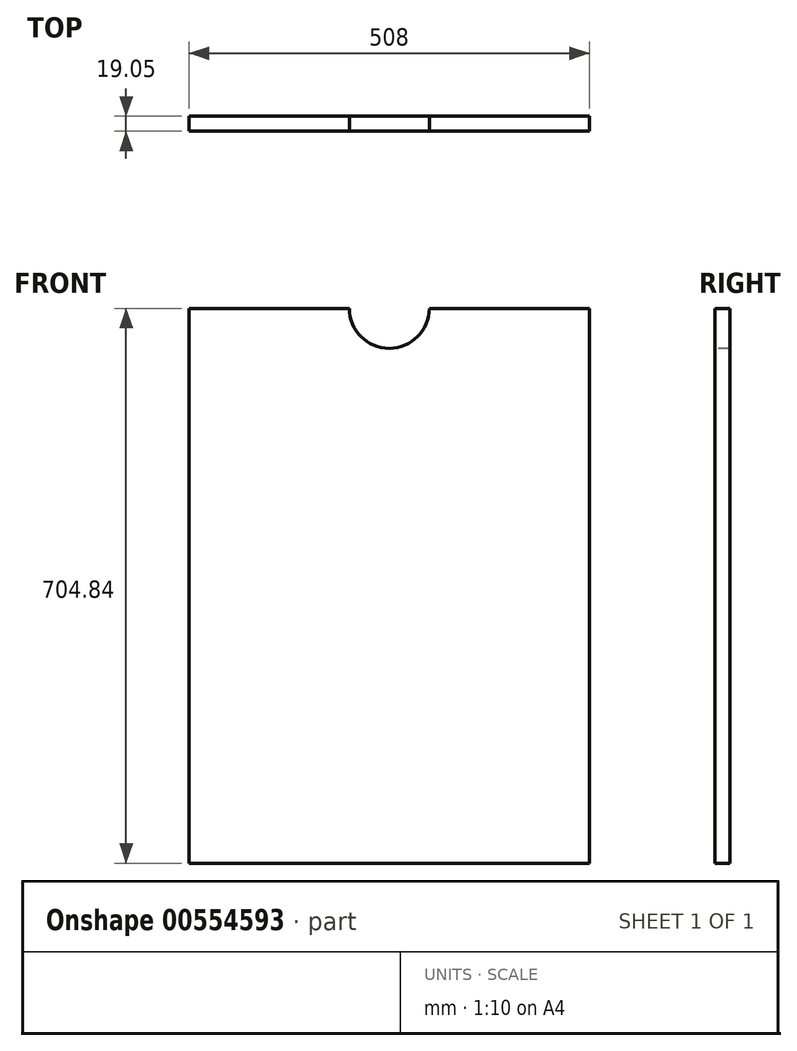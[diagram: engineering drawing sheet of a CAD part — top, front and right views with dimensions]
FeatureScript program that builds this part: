
annotation { "Feature Type Name" : "Feature", "Feature Type Description" : "" }
export const myFeature = defineFeature(function(context is Context, id is Id, definition is map)
    precondition{}
    {
        {
            var Q0;
            Q0=qCreatedBy(makeId("Front.planeOp"),FACE);
            var sketch = newSketch(context, id + "F0", { "sketchPlane" : qUnion([Q0])});
            skLineSegment(sketch, "E0.bottom", {"start": v(254, 517.52) * mm, "end": v(-254, 517.52) * mm});
            skLineSegment(sketch, "E0.top", {"start": v(254, -517.52) * mm, "end": v(-254, -517.52) * mm});
            skLineSegment(sketch, "E0.left", {"start": v(254, 517.52) * mm, "end": v(254, -517.52) * mm});
            skLineSegment(sketch, "E0.right", {"start": v(-254, 517.52) * mm, "end": v(-254, -517.52) * mm});
            skPoint(sketch, "E0.middle", {"position": v(0, 0) * mm});
            skSolve(sketch);
        }
        {
            var Q0;
            Q0=makeQuery(id+"F0.imprint","IMPRINT",FACE,{"disambiguationData":[TD([[makeQuery(id+"F0.imprint","IMPRINT",EDGE,{"derivedFrom":sQuery(id+"F0.wireOp",EDGE,"E0.bottom")}),1.0]])]});
            extrude(context, id + "F1", {"entities" : qUnion([Q0]), "depth" : 19.05 * mm, "offsetDistance" : 25.4 * mm});
        }
        {
            var Q0;
            Q0=makeQuery(id+"F1.opExtrude","CAP_FACE",FACE,{"disambiguationData":[OSD([sQuery(id+"F0.wireOp",EDGE,"E0.bottom"),sQuery(id+"F0.wireOp",EDGE,"E0.top"),sQuery(id+"F0.wireOp",EDGE,"E0.left"),sQuery(id+"F0.wireOp",EDGE,"E0.right")])],"isStart":false});
            var sketch = newSketch(context, id + "F2", { "sketchPlane" : qUnion([Q0])});
            skCircle(sketch, "E1", {"center": v(0, 517.52) * mm, "radius": 50.8 * mm});
            skSolve(sketch);
        }
        {
            var Q0;
            {var subQ0=sQuery(id+"F2.wireOp",EDGE,"E1");var subQ1=makeQuery(id+"F1.opExtrude","CAP_EDGE",EDGE,{"disambiguationData":[OSD([sQuery(id+"F0.wireOp",EDGE,"E0.bottom")])],"isStart":false});var subQ2=makeQuery(id+"F2.imprint","INTERSECT",VERTEX,{"disambiguationData":[OD(0.0)],"derivedFrom":[subQ1,subQ0]});Q0=makeQuery(id+"F2.imprint","IMPRINT",FACE,{"disambiguationData":[TD([[makeQuery(id+"F2.imprint","IMPRINT",EDGE,{"disambiguationData":[TD([[subQ2,1.0]])],"derivedFrom":subQ0}),1.0]])]});}
            extrude(context, id + "F3", {"entities" : qUnion([Q0]), "operationType" : NewBodyOperationType.REMOVE, "oppositeDirection" : true, "depth" : 25.4 * mm, "offsetDistance" : 25.4 * mm});
        }
        {
            var Q0;
            Q0=makeQuery(id+"F1.opExtrude","SWEPT_FACE",FACE,{"disambiguationData":[OSD([sQuery(id+"F0.wireOp",EDGE,"E0.top")])]});
            extrude(context, id + "F4", {"entities" : qUnion([Q0]), "operationType" : NewBodyOperationType.REMOVE, "oppositeDirection" : true, "depth" : 330.2 * mm, "offsetDistance" : 25.4 * mm});
        }
    });
